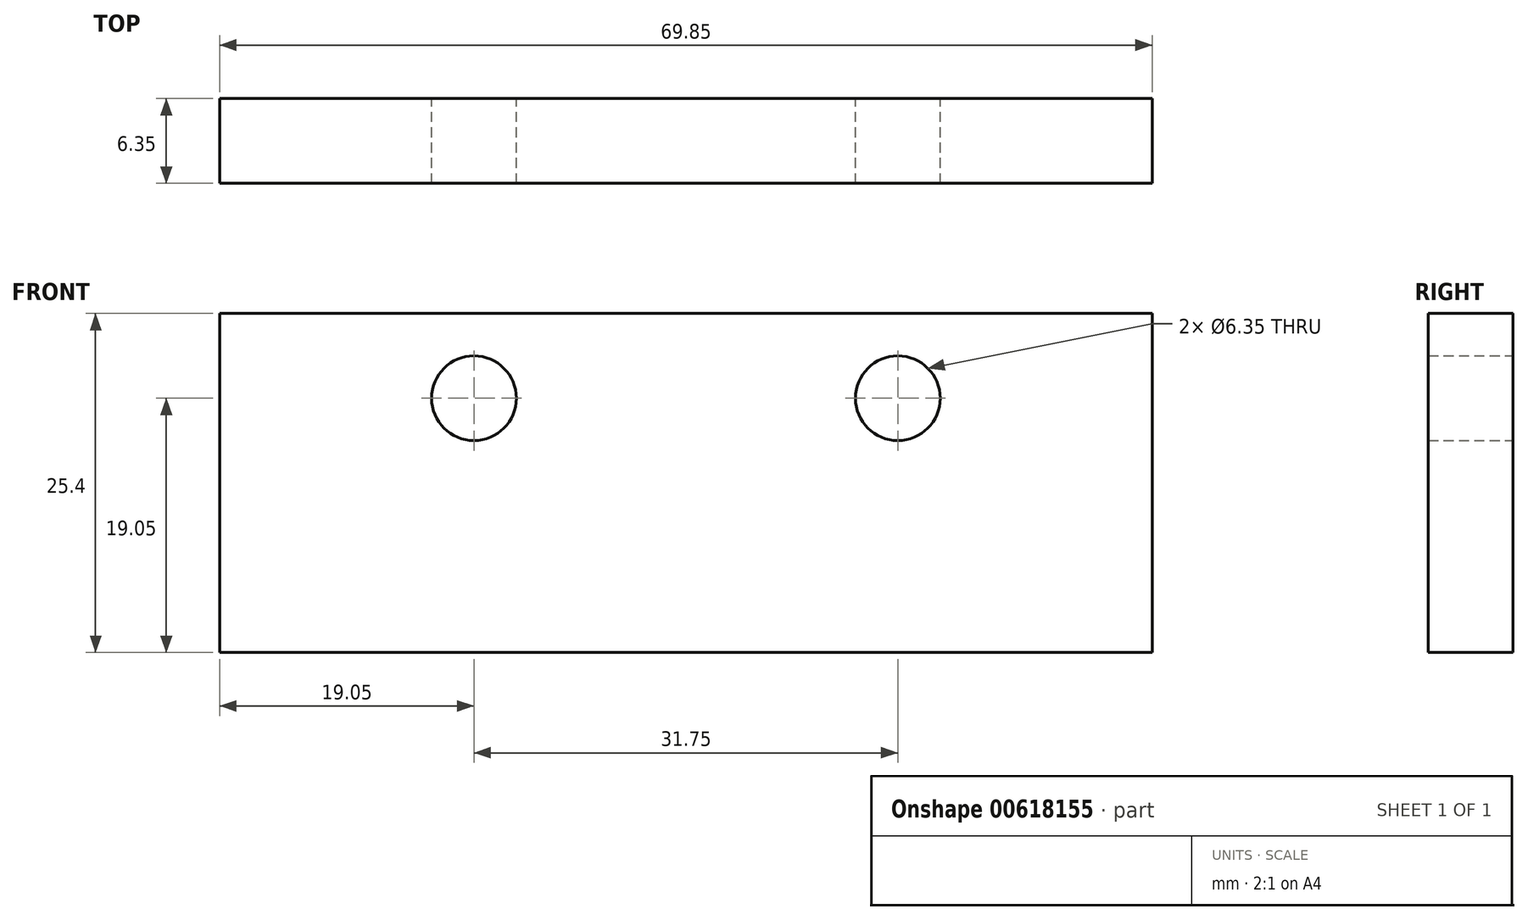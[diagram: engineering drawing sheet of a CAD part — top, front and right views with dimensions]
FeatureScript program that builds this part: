
annotation { "Feature Type Name" : "Feature", "Feature Type Description" : "" }
export const myFeature = defineFeature(function(context is Context, id is Id, definition is map)
    precondition{}
    {
        {
            var Q0;
            Q0=qCreatedBy(makeId("Front.planeOp"),FACE);
            var sketch = newSketch(context, id + "F0", { "sketchPlane" : qUnion([Q0])});
            skLineSegment(sketch, "E0.bottom", {"start": v(0, 0) * mm, "end": v(69.85, 0) * mm});
            skLineSegment(sketch, "E0.top", {"start": v(0, 25.4) * mm, "end": v(69.85, 25.4) * mm});
            skLineSegment(sketch, "E0.left", {"start": v(0, 0) * mm, "end": v(0, 25.4) * mm});
            skLineSegment(sketch, "E0.right", {"start": v(69.85, 0) * mm, "end": v(69.85, 25.4) * mm});
            skCircle(sketch, "E1", {"center": v(19.05, 19.05) * mm, "radius": 3.18 * mm});
            skCircle(sketch, "E2", {"center": v(50.8, 19.05) * mm, "radius": 3.18 * mm});
            skSolve(sketch);
        }
        {
            var Q0;
            Q0=qSketchRegion(id+"F0",true);
            extrude(context, id + "F1", {"entities" : qUnion([Q0]), "depth" : 6.35 * mm});
        }
    });
